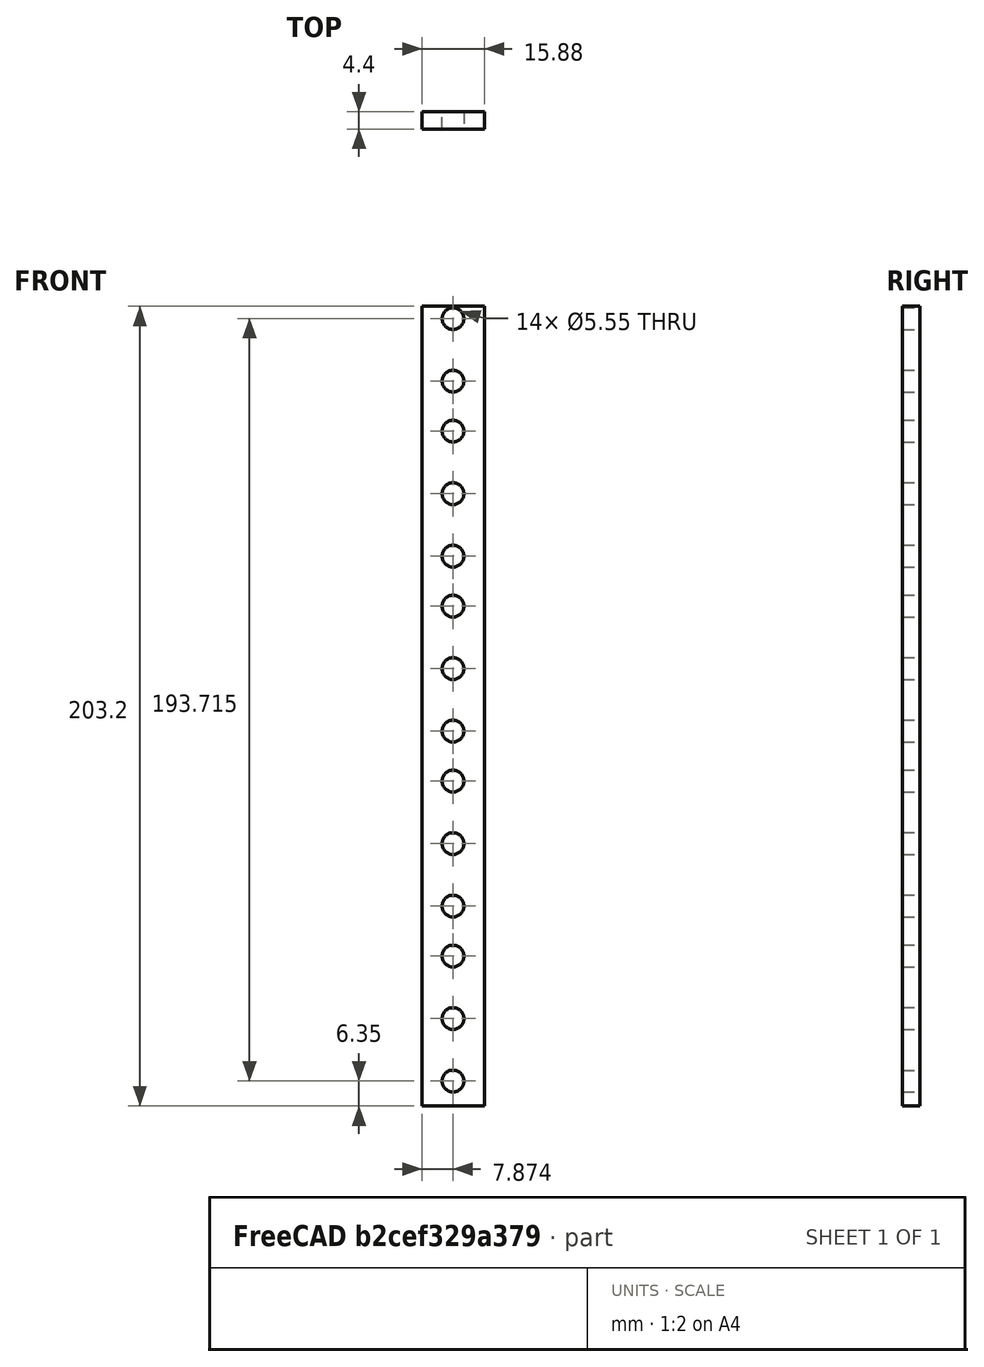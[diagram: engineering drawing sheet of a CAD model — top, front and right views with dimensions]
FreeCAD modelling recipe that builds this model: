
FCSTD DOCUMENT  (FreeCAD 0.19R14555 (Git shallow))
Label: 4.5U_Rail_v0
License: All rights reserved
LicenseURL: http://en.wikipedia.org/wiki/All_rights_reserved
objects: Sketcher::SketchObject×1, PartDesign::Pad×1, PartDesign::Body×1
note: 4 computed .brp shape members not serialized (recipe doc carries the construction recipe); baked Part::Feature solids carry a one-line shape summary decoded from their .brp

FEATURE [Sketcher::SketchObject] Sketch
  FullyConstrained = true
  MapMode = 5
  Placement = pos=(0,0,0) rot=(1,0,0;1.5708rad)
  Support = -> [XZ_Plane]
  sketch-geometry (18):
    g0: LineSegment StartX=0 StartY=0 StartZ=0 EndX=15.875 EndY=0 EndZ=0
    g1: LineSegment StartX=15.875 StartY=0 StartZ=0 EndX=15.875 EndY=203.2 EndZ=0
    g2: LineSegment StartX=15.875 StartY=203.2 StartZ=0 EndX=0 EndY=203.2 EndZ=0
    g3: LineSegment StartX=0 StartY=203.2 StartZ=0 EndX=0 EndY=0 EndZ=0
    g4: Circle CenterX=7.874 CenterY=6.35 CenterZ=0 NormalX=0 NormalY=0 NormalZ=1 AngleXU=0 Radius=2.775
    g5: Circle CenterX=7.874 CenterY=22.23 CenterZ=0 NormalX=0 NormalY=0 NormalZ=1 AngleXU=0 Radius=2.775
    g6: Circle CenterX=7.874 CenterY=38.11 CenterZ=0 NormalX=0 NormalY=0 NormalZ=1 AngleXU=0 Radius=2.775
    g7: Circle CenterX=7.874 CenterY=50.81 CenterZ=0 NormalX=0 NormalY=0 NormalZ=1 AngleXU=0 Radius=2.775
    g8: Circle CenterX=7.874 CenterY=66.69 CenterZ=0 NormalX=0 NormalY=0 NormalZ=1 AngleXU=0 Radius=2.775
    g9: Circle CenterX=7.874 CenterY=82.57 CenterZ=0 NormalX=0 NormalY=0 NormalZ=1 AngleXU=0 Radius=2.775
    g10: Circle CenterX=7.874 CenterY=95.27 CenterZ=0 NormalX=0 NormalY=0 NormalZ=1 AngleXU=0 Radius=2.775
    g11: Circle CenterX=7.874 CenterY=111.15 CenterZ=0 NormalX=0 NormalY=0 NormalZ=1 AngleXU=0 Radius=2.775
    g12: Circle CenterX=7.874 CenterY=127.03 CenterZ=0 NormalX=0 NormalY=0 NormalZ=1 AngleXU=0 Radius=2.775
    g13: Circle CenterX=7.874 CenterY=139.73 CenterZ=0 NormalX=0 NormalY=0 NormalZ=1 AngleXU=0 Radius=2.775
    g14: Circle CenterX=7.874 CenterY=155.61 CenterZ=0 NormalX=0 NormalY=0 NormalZ=1 AngleXU=0 Radius=2.775
    g15: Circle CenterX=7.874 CenterY=171.49 CenterZ=0 NormalX=0 NormalY=0 NormalZ=1 AngleXU=0 Radius=2.775
    g16: Circle CenterX=7.874 CenterY=184.19 CenterZ=0 NormalX=0 NormalY=0 NormalZ=1 AngleXU=0 Radius=2.775
    g17: Circle CenterX=7.874 CenterY=200.065 CenterZ=0 NormalX=0 NormalY=0 NormalZ=1 AngleXU=0 Radius=2.775
  constraints (53):
    c: Coincident(g0,g1)
    c: Coincident(g1,g2)
    c: Coincident(g2,g3)
    c: Coincident(g3,g0)
    c: Horizontal(g0)
    c: Horizontal(g2)
    c: Vertical(g1)
    c: Vertical(g3)
    c: Coincident(g0,g-1)
    c: DistanceX(g2,g2) = 15.875
    c: DistanceY(g3,g3) = 203.2
    c: Diameter(g4) = 5.55
    c: DistanceX(g0,g4) = 7.874
    c: DistanceY(g0,g4) = 6.35
    c: Equal(g4,g5) = 5.55
    c: Vertical(g5,g4)
    c: DistanceY(g4,g5) = 15.88
    c: Vertical(g6,g5)
    c: DistanceY(g5,g6) = 15.88
    c: Diameter(g6) = 5.55
    c: Equal(g4,g7) = 5.55
    c: Equal(g7,g8) = 5.55
    c: Vertical(g8,g7)
    c: DistanceY(g7,g8) = 15.88
    c: Vertical(g9,g8)
    c: DistanceY(g8,g9) = 15.88
    c: Equal(g6,g9) = 5.55
    c: DistanceY(g6,g7) = 12.7
    c: Vertical(g6,g7)
    c: Equal(g4,g10) = 5.55
    c: Equal(g10,g11) = 5.55
    c: Vertical(g11,g10)
    c: DistanceY(g10,g11) = 15.88
    c: Vertical(g12,g11)
    c: DistanceY(g11,g12) = 15.88
    c: Equal(g6,g12) = 5.55
    c: Equal(g10,g13) = 5.55
    c: Equal(g13,g14) = 5.55
    c: Vertical(g14,g13)
    c: DistanceY(g13,g14) = 15.88
    c: Vertical(g15,g14)
    c: DistanceY(g14,g15) = 15.88
    c: Equal(g12,g15) = 5.55
    c: DistanceY(g12,g13) = 12.7
    c: Vertical(g12,g13)
    c: DistanceY(g9,g10) = 12.7
    c: Vertical(g9,g10)
    c: Vertical(g15,g16)
    c: DistanceY(g15,g16) = 12.7
    c: Vertical(g16,g17)
    c: DistanceY(g16,g17) = 15.875
    c: Diameter(g16) = 5.55
    c: Diameter(g17) = 5.55
FEATURE [PartDesign::Pad] Pad
  Direction = (1,1,1)
  Length = 4.4
  Length2 = 100
  Placement = pos=(0,0,0) rot=(1,0,0;1.5708rad)
  Profile = -> Sketch
  Refine = true
  Type = 0
FEATURE [PartDesign::Body] Body
  Group = -> [Sketch,Pad]
  Origin = -> Origin
  Tip = -> Pad
